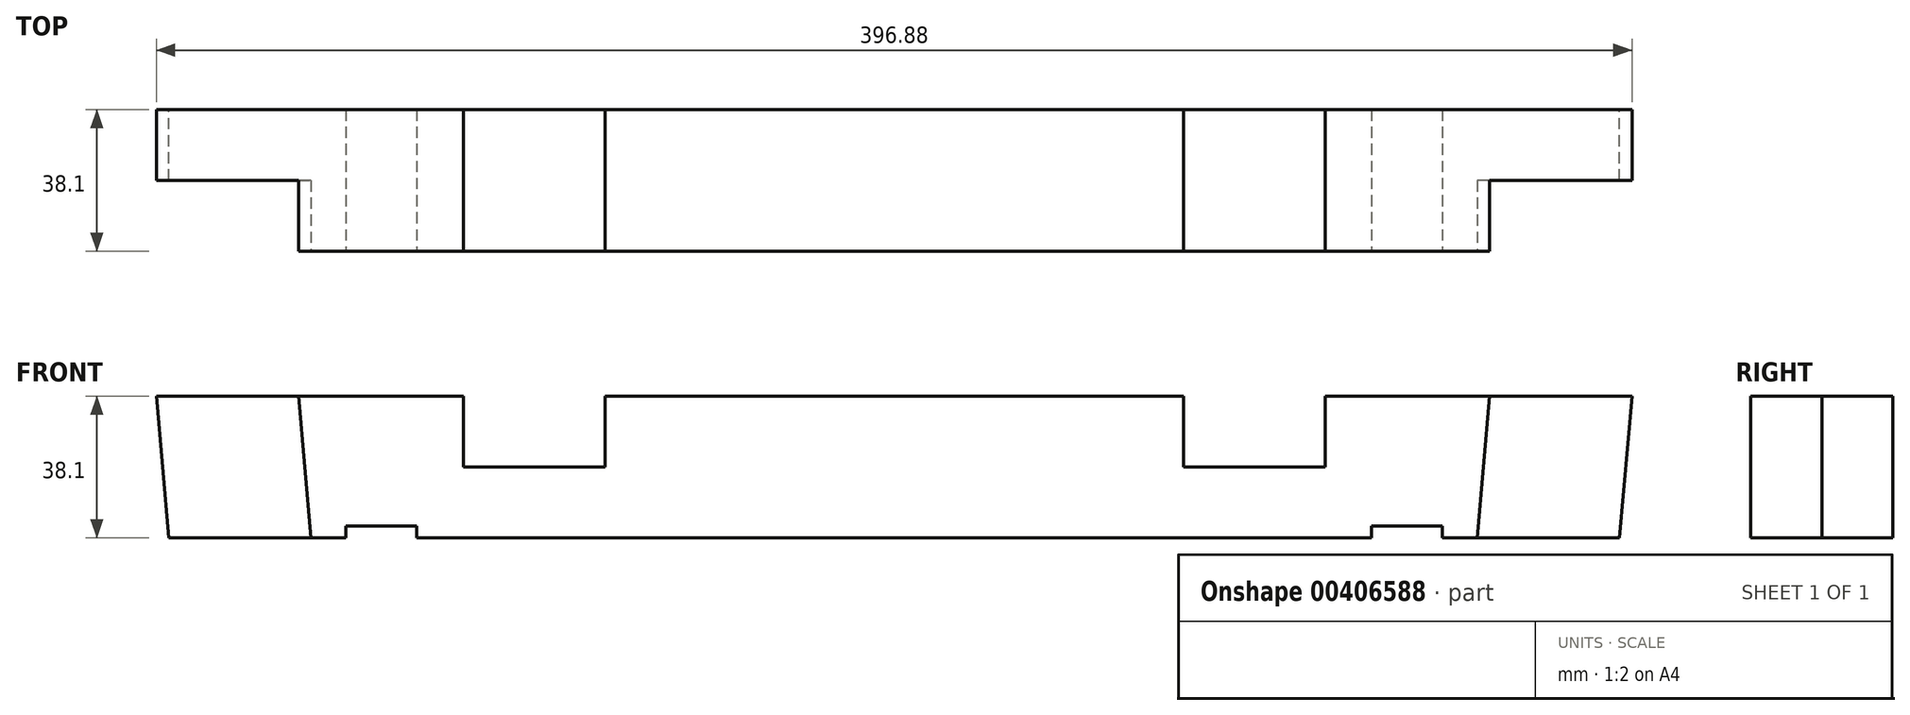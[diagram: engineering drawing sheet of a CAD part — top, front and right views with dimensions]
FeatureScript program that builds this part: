
annotation { "Feature Type Name" : "Feature", "Feature Type Description" : "" }
export const myFeature = defineFeature(function(context is Context, id is Id, definition is map)
    precondition{}
    {
        {
            var Q0;
            Q0=qCreatedBy(makeId("Front.planeOp"),FACE);
            var sketch = newSketch(context, id + "F0", { "sketchPlane" : qUnion([Q0])});
            skLineSegment(sketch, "E0", {"start": v(0, 0) * mm, "end": v(396.88, 0) * mm});
            skLineSegment(sketch, "E1", {"start": v(396.88, 0) * mm, "end": v(393.54, -38.1) * mm});
            skLineSegment(sketch, "E2", {"start": v(393.54, -38.1) * mm, "end": v(3.33, -38.1) * mm});
            skLineSegment(sketch, "E3", {"start": v(3.33, -38.1) * mm, "end": v(0, 0) * mm});
            skSolve(sketch);
        }
        {
            var Q0;
            Q0=makeQuery(id+"F0.imprint","IMPRINT",FACE,{"disambiguationData":[TD([[makeQuery(id+"F0.imprint","IMPRINT",EDGE,{"derivedFrom":sQuery(id+"F0.wireOp",EDGE,"E0")}),-1.0]])]});
            extrude(context, id + "F1", {"entities" : qUnion([Q0]), "depth" : 38.1 * mm});
        }
        {
            var Q0;
            Q0=makeQuery(id+"F1.opExtrude","CAP_FACE",FACE,{"disambiguationData":[OSD([sQuery(id+"F0.wireOp",EDGE,"E0"),sQuery(id+"F0.wireOp",EDGE,"E1"),sQuery(id+"F0.wireOp",EDGE,"E2"),sQuery(id+"F0.wireOp",EDGE,"E3")])],"isStart":false});
            var sketch = newSketch(context, id + "F2", { "sketchPlane" : qUnion([Q0])});
            skLineSegment(sketch, "E4", {"start": v(358.63, 0) * mm, "end": v(355.3, -38.1) * mm});
            skLineSegment(sketch, "E5", {"start": v(358.63, 0) * mm, "end": v(396.88, 0) * mm});
            skLineSegment(sketch, "E6", {"start": v(396.88, 0) * mm, "end": v(393.54, -38.1) * mm});
            skLineSegment(sketch, "E7", {"start": v(393.54, -38.1) * mm, "end": v(355.3, -38.1) * mm});
            skSolve(sketch);
        }
        {
            var Q0;
            Q0=makeQuery(id+"F2.imprint","IMPRINT",FACE,{"disambiguationData":[TD([[makeQuery(id+"F2.imprint","IMPRINT",EDGE,{"derivedFrom":sQuery(id+"F2.wireOp",EDGE,"E4")}),1.0]])]});
            extrude(context, id + "F3", {"entities" : qUnion([Q0]), "operationType" : NewBodyOperationType.REMOVE, "oppositeDirection" : true, "depth" : 19.05 * mm});
        }
        {
            var Q0;
            Q0=makeQuery(id+"F1.opExtrude","CAP_FACE",FACE,{"disambiguationData":[OSD([sQuery(id+"F0.wireOp",EDGE,"E0"),sQuery(id+"F0.wireOp",EDGE,"E1"),sQuery(id+"F0.wireOp",EDGE,"E2"),sQuery(id+"F0.wireOp",EDGE,"E3")])],"isStart":false});
            var sketch = newSketch(context, id + "F4", { "sketchPlane" : qUnion([Q0])});
            skLineSegment(sketch, "E8", {"start": v(38.25, 0) * mm, "end": v(41.58, -38.1) * mm});
            skLineSegment(sketch, "E9", {"start": v(38.25, 0) * mm, "end": v(0, 0) * mm});
            skLineSegment(sketch, "E10", {"start": v(0, 0) * mm, "end": v(3.33, -38.1) * mm});
            skLineSegment(sketch, "E11", {"start": v(3.33, -38.1) * mm, "end": v(41.58, -38.1) * mm});
            skSolve(sketch);
        }
        {
            var Q0;
            Q0=makeQuery(id+"F4.imprint","IMPRINT",FACE,{"disambiguationData":[TD([[makeQuery(id+"F4.imprint","IMPRINT",EDGE,{"derivedFrom":sQuery(id+"F4.wireOp",EDGE,"E8")}),-1.0]])]});
            extrude(context, id + "F5", {"entities" : qUnion([Q0]), "operationType" : NewBodyOperationType.REMOVE, "oppositeDirection" : true, "depth" : 19.05 * mm});
        }
        {
            var Q0;
            Q0=makeQuery(id+"F1.opExtrude","CAP_FACE",FACE,{"disambiguationData":[OSD([sQuery(id+"F0.wireOp",EDGE,"E0"),sQuery(id+"F0.wireOp",EDGE,"E1"),sQuery(id+"F0.wireOp",EDGE,"E2"),sQuery(id+"F0.wireOp",EDGE,"E3")])],"isStart":false});
            var sketch = newSketch(context, id + "F6", { "sketchPlane" : qUnion([Q0])});
            skLineSegment(sketch, "E12.bottom", {"start": v(276.23, 0) * mm, "end": v(314.33, 0) * mm});
            skLineSegment(sketch, "E12.top", {"start": v(276.23, -19.05) * mm, "end": v(314.33, -19.05) * mm});
            skLineSegment(sketch, "E12.left", {"start": v(276.23, 0) * mm, "end": v(276.23, -19.05) * mm});
            skLineSegment(sketch, "E12.right", {"start": v(314.33, 0) * mm, "end": v(314.33, -19.05) * mm});
            skSolve(sketch);
        }
        {
            var Q0;
            Q0=makeQuery(id+"F6.imprint","IMPRINT",FACE,{"disambiguationData":[TD([[makeQuery(id+"F6.imprint","IMPRINT",EDGE,{"derivedFrom":sQuery(id+"F6.wireOp",EDGE,"E12.bottom")}),-1.0]])]});
            extrude(context, id + "F7", {"entities" : qUnion([Q0]), "operationType" : NewBodyOperationType.REMOVE, "oppositeDirection" : true, "depth" : 38.1 * mm});
        }
        {
            var Q0;
            Q0=makeQuery(id+"F1.opExtrude","CAP_FACE",FACE,{"disambiguationData":[OSD([sQuery(id+"F0.wireOp",EDGE,"E0"),sQuery(id+"F0.wireOp",EDGE,"E1"),sQuery(id+"F0.wireOp",EDGE,"E2"),sQuery(id+"F0.wireOp",EDGE,"E3")])],"isStart":false});
            var sketch = newSketch(context, id + "F8", { "sketchPlane" : qUnion([Q0])});
            skLineSegment(sketch, "E13.bottom", {"start": v(50.96, -38.1) * mm, "end": v(70, -38.1) * mm});
            skLineSegment(sketch, "E13.top", {"start": v(50.96, -34.93) * mm, "end": v(70, -34.93) * mm});
            skLineSegment(sketch, "E13.left", {"start": v(50.96, -38.1) * mm, "end": v(50.96, -34.93) * mm});
            skLineSegment(sketch, "E13.right", {"start": v(70, -38.1) * mm, "end": v(70, -34.93) * mm});
            skSolve(sketch);
        }
        {
            var Q0;
            Q0=makeQuery(id+"F8.imprint","IMPRINT",FACE,{"disambiguationData":[TD([[makeQuery(id+"F8.imprint","IMPRINT",EDGE,{"derivedFrom":sQuery(id+"F8.wireOp",EDGE,"E13.bottom")}),-1.0]])]});
            extrude(context, id + "F9", {"entities" : qUnion([Q0]), "operationType" : NewBodyOperationType.REMOVE, "oppositeDirection" : true, "depth" : 38.1 * mm});
        }
        {
            var Q0;
            Q0=makeQuery(id+"F1.opExtrude","CAP_FACE",FACE,{"disambiguationData":[OSD([sQuery(id+"F0.wireOp",EDGE,"E0"),sQuery(id+"F0.wireOp",EDGE,"E1"),sQuery(id+"F0.wireOp",EDGE,"E2"),sQuery(id+"F0.wireOp",EDGE,"E3")])],"isStart":false});
            var sketch = newSketch(context, id + "F10", { "sketchPlane" : qUnion([Q0])});
            skLineSegment(sketch, "E14.bottom", {"start": v(326.87, -38.1) * mm, "end": v(345.92, -38.1) * mm});
            skLineSegment(sketch, "E14.top", {"start": v(326.87, -34.92) * mm, "end": v(345.92, -34.92) * mm});
            skLineSegment(sketch, "E14.left", {"start": v(326.87, -38.1) * mm, "end": v(326.87, -34.92) * mm});
            skLineSegment(sketch, "E14.right", {"start": v(345.92, -38.1) * mm, "end": v(345.92, -34.92) * mm});
            skSolve(sketch);
        }
        {
            var Q0;
            Q0=makeQuery(id+"F10.imprint","IMPRINT",FACE,{"disambiguationData":[TD([[makeQuery(id+"F10.imprint","IMPRINT",EDGE,{"derivedFrom":sQuery(id+"F10.wireOp",EDGE,"E14.bottom")}),-1.0]])]});
            extrude(context, id + "F11", {"entities" : qUnion([Q0]), "operationType" : NewBodyOperationType.REMOVE, "oppositeDirection" : true, "depth" : 38.1 * mm});
        }
        {
            var Q0;
            Q0=makeQuery(id+"F1.opExtrude","CAP_FACE",FACE,{"disambiguationData":[OSD([sQuery(id+"F0.wireOp",EDGE,"E0"),sQuery(id+"F0.wireOp",EDGE,"E1"),sQuery(id+"F0.wireOp",EDGE,"E2"),sQuery(id+"F0.wireOp",EDGE,"E3")])],"isStart":false});
            var sketch = newSketch(context, id + "F12", { "sketchPlane" : qUnion([Q0])});
            skLineSegment(sketch, "E15.bottom", {"start": v(82.55, 0) * mm, "end": v(120.65, 0) * mm});
            skLineSegment(sketch, "E15.top", {"start": v(82.55, -19.05) * mm, "end": v(120.65, -19.05) * mm});
            skLineSegment(sketch, "E15.left", {"start": v(82.55, 0) * mm, "end": v(82.55, -19.05) * mm});
            skLineSegment(sketch, "E15.right", {"start": v(120.65, 0) * mm, "end": v(120.65, -19.05) * mm});
            skSolve(sketch);
        }
        {
            var Q0;
            Q0=makeQuery(id+"F12.imprint","IMPRINT",FACE,{"disambiguationData":[TD([[makeQuery(id+"F12.imprint","IMPRINT",EDGE,{"derivedFrom":sQuery(id+"F12.wireOp",EDGE,"E15.bottom")}),-1.0]])]});
            extrude(context, id + "F13", {"entities" : qUnion([Q0]), "operationType" : NewBodyOperationType.REMOVE, "oppositeDirection" : true, "depth" : 38.1 * mm});
        }
    });
